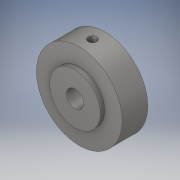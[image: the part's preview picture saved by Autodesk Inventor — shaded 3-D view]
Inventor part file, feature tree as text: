
AUTODESK INVENTOR PART (.ipt)
format: ipt  version: 2018 (Build 220112000, 112)  size: 124,416 bytes
history: native  units: in
note: dims shown in document units (in); Inventor stores cm internally (conversion verified against a paired STEP export)
features: extrude x4, sketch x4
ambient origin geometry x8: Origin, YZ Plane, XZ Plane, XY Plane, X Axis, Y Axis, Z Axis, Center Point
bodies: Solid1 (feature_tree)
feature tree (8):
  extrude  "Extrusion1"  Depth=0.375in TaperAngle=0.0deg
  extrude  "Extrusion2"  Depth=0.0625in TaperAngle=0.0deg
  extrude  "Extrusion3"  Depth=1.0in TaperAngle=0.0deg
  extrude  "Extrusion4"  Depth=0.125in TaperAngle=0.0deg
  sketch  "Sketch1"  dims[d0=1.25in d2=0.375in d3=0.0in]
  sketch  "Sketch2"  dims[d4=0.74in d5=0.0625in d6=0.0in]
  sketch  "Sketch3"  dims[d7=0.25in d8=1.0in d9=0.0in]
  sketch  "Sketch4"  dims[d10=0.125in d11=1.0in d12=0.0in]
